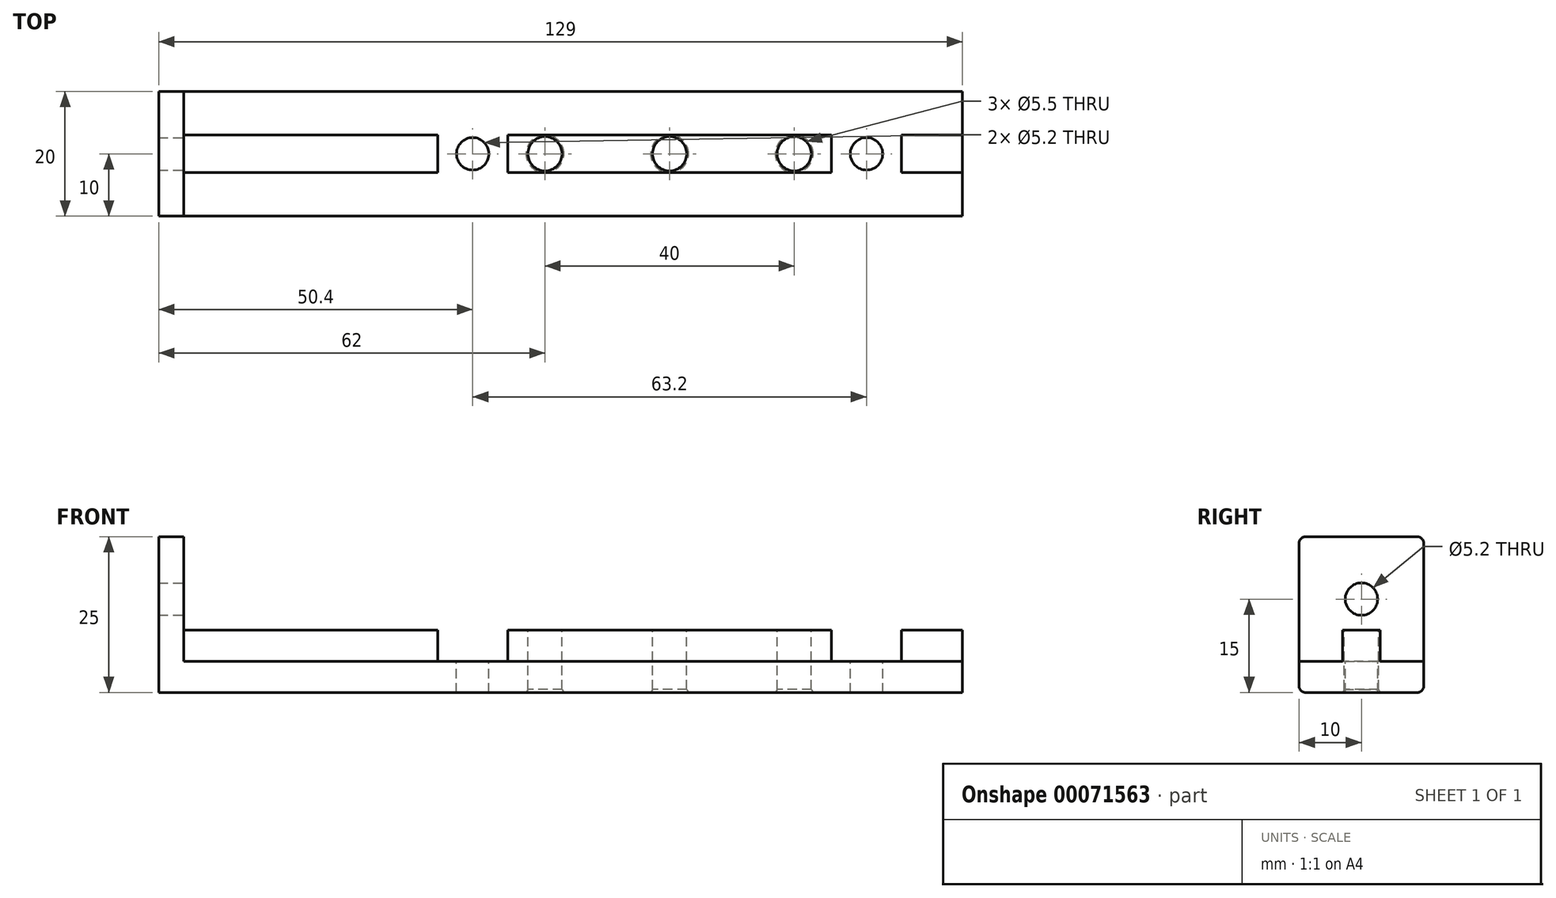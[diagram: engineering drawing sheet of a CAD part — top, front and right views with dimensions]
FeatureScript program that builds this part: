
annotation { "Feature Type Name" : "Feature", "Feature Type Description" : "" }
export const myFeature = defineFeature(function(context is Context, id is Id, definition is map)
    precondition{}
    {
        {
            var Q0;
            Q0=qCreatedBy(makeId("Top.planeOp"),FACE);
            var sketch = newSketch(context, id + "F0", { "sketchPlane" : qUnion([Q0])});
            skLineSegment(sketch, "E0.bottom", {"start": v(0, -10) * mm, "end": v(125, -10) * mm});
            skLineSegment(sketch, "E0.top", {"start": v(0, 10) * mm, "end": v(125, 10) * mm});
            skLineSegment(sketch, "E0.left", {"start": v(0, -10) * mm, "end": v(0, 10) * mm});
            skLineSegment(sketch, "E0.right", {"start": v(125, -10) * mm, "end": v(125, 10) * mm});
            skSolve(sketch);
        }
        {
            var Q0;
            Q0 = qSketchRegion(id + "F0", true);
            extrude(context, id + "F1", {"entities" : qUnion([Q0]), "depth" : 5 * mm});
        }
        {
            var Q0;
            Q0=makeQuery(id+"F1.opExtrude","CAP_FACE",FACE,{"disambiguationData":[OSD([sQuery(id+"F0.wireOp",EDGE,"E0.bottom"),sQuery(id+"F0.wireOp",EDGE,"E0.top"),sQuery(id+"F0.wireOp",EDGE,"E0.left"),sQuery(id+"F0.wireOp",EDGE,"E0.right")])],"isStart":false});
            var sketch = newSketch(context, id + "F2", { "sketchPlane" : qUnion([Q0])});
            skLineSegment(sketch, "E1.bottom", {"start": v(0, 3) * mm, "end": v(125, 3) * mm});
            skLineSegment(sketch, "E1.top", {"start": v(0, -3) * mm, "end": v(125, -3) * mm});
            skLineSegment(sketch, "E1.left", {"start": v(0, 3) * mm, "end": v(0, -3) * mm});
            skLineSegment(sketch, "E1.right", {"start": v(125, 3) * mm, "end": v(125, -3) * mm});
            skSolve(sketch);
        }
        {
            var Q0;
            Q0 = qSketchRegion(id + "F2", true);
            extrude(context, id + "F3", {"entities" : qUnion([Q0]), "operationType" : NewBodyOperationType.ADD, "depth" : 5 * mm});
        }
        {
            var Q0;
            Q0=makeQuery(id+"F3.opExtrude","CAP_FACE",FACE,{"disambiguationData":[OSD([sQuery(id+"F2.wireOp",EDGE,"E1.bottom"),sQuery(id+"F2.wireOp",EDGE,"E1.top"),sQuery(id+"F2.wireOp",EDGE,"E1.left"),sQuery(id+"F2.wireOp",EDGE,"E1.right")])],"isStart":false});
            var sketch = newSketch(context, id + "F4", { "sketchPlane" : qUnion([Q0])});
            skLineSegment(sketch, "E2", {"start": v(0, 0) * mm, "end": v(58, 0) * mm, "construction": true});
            skLineSegment(sketch, "E3", {"start": v(58, 0) * mm, "end": v(78, 0) * mm, "construction": true});
            skLineSegment(sketch, "E4", {"start": v(78, 0) * mm, "end": v(98, 0) * mm, "construction": true});
            skCircle(sketch, "E5", {"center": v(98, 0) * mm, "radius": 2.75 * mm});
            skCircle(sketch, "E6", {"center": v(78, 0) * mm, "radius": 2.75 * mm});
            skCircle(sketch, "E7", {"center": v(58, 0) * mm, "radius": 2.75 * mm});
            skSolve(sketch);
        }
        {
            var Q0;
            Q0 = qSketchRegion(id + "F4", true);
            extrude(context, id + "F5", {"entities" : qUnion([Q0]), "operationType" : NewBodyOperationType.REMOVE, "oppositeDirection" : true, "depth" : 25 * mm});
        }
        {
            var Q0;
            Q0=makeQuery(id+"F3.opExtrude","CAP_FACE",FACE,{"disambiguationData":[OSD([sQuery(id+"F2.wireOp",EDGE,"E1.bottom"),sQuery(id+"F2.wireOp",EDGE,"E1.top"),sQuery(id+"F2.wireOp",EDGE,"E1.left"),sQuery(id+"F2.wireOp",EDGE,"E1.right")])],"isStart":false});
            var sketch = newSketch(context, id + "F6", { "sketchPlane" : qUnion([Q0])});
            skLineSegment(sketch, "E8.bottom", {"start": v(104, 3) * mm, "end": v(115.2, 3) * mm});
            skLineSegment(sketch, "E8.top", {"start": v(104, -3) * mm, "end": v(115.2, -3) * mm});
            skLineSegment(sketch, "E8.left", {"start": v(104, 3) * mm, "end": v(104, -3) * mm});
            skLineSegment(sketch, "E8.right", {"start": v(115.2, 3) * mm, "end": v(115.2, -3) * mm});
            skLineSegment(sketch, "E9.bottom", {"start": v(40.8, 3) * mm, "end": v(52, 3) * mm});
            skLineSegment(sketch, "E9.top", {"start": v(40.8, -3) * mm, "end": v(52, -3) * mm});
            skLineSegment(sketch, "E9.left", {"start": v(40.8, 3) * mm, "end": v(40.8, -3) * mm});
            skLineSegment(sketch, "E9.right", {"start": v(52, 3) * mm, "end": v(52, -3) * mm});
            skLineSegment(sketch, "E10", {"start": v(58, 0) * mm, "end": v(52, 0) * mm, "construction": true});
            skLineSegment(sketch, "E11", {"start": v(98, 0) * mm, "end": v(104, 0) * mm, "construction": true});
            skSolve(sketch);
        }
        {
            var Q0;
            Q0 = qSketchRegion(id + "F6", true);
            var Q1;
            {var subQ0=sQuery(id+"F0.wireOp",EDGE,"E0.right");var subQ1=sQuery(id+"F0.wireOp",EDGE,"E0.left");var subQ2=sQuery(id+"F0.wireOp",EDGE,"E0.top");Q1=makeQuery(id+"F3.boolean.opBoolean","SPLIT",FACE,{"disambiguationData":[TD([makeQuery(id+"F1.opExtrude","SWEPT_FACE",FACE,{"disambiguationData":[OSD([subQ2])]})])],"derivedFrom":makeQuery(id+"F1.opExtrude","CAP_FACE",FACE,{"disambiguationData":[OSD([sQuery(id+"F0.wireOp",EDGE,"E0.bottom"),subQ2,subQ1,subQ0])],"isStart":false})});}
            extrude(context, id + "F7", {"entities" : qUnion([Q0]), "operationType" : NewBodyOperationType.REMOVE, "endBound" : BoundingType.UP_TO_SURFACE, "oppositeDirection" : true, "endBoundEntityFace" : qUnion([Q1]), "depth" : 25 * mm});
        }
        {
            var Q0;
            {var subQ0=sQuery(id+"F0.wireOp",EDGE,"E0.right");var subQ3=sQuery(id+"F0.wireOp",EDGE,"E0.left");var subQ5=sQuery(id+"F0.wireOp",EDGE,"E0.top");var subQ7=sQuery(id+"F0.wireOp",EDGE,"E0.bottom");var subQ8=makeQuery(id+"F1.opExtrude","CAP_FACE",FACE,{"disambiguationData":[OSD([subQ7,subQ5,subQ3,subQ0])],"isStart":false});Q0=makeQuery(id+"F7.boolean.opBoolean","MERGE",FACE,{"derivedFrom":[makeQuery(id+"F3.boolean.opBoolean","SPLIT",FACE,{"disambiguationData":[TD([makeQuery(id+"F1.opExtrude","SWEPT_FACE",FACE,{"disambiguationData":[OSD([subQ7])]})])],"derivedFrom":subQ8}),makeQuery(id+"F3.boolean.opBoolean","SPLIT",FACE,{"disambiguationData":[TD([makeQuery(id+"F1.opExtrude","SWEPT_FACE",FACE,{"disambiguationData":[OSD([subQ5])]})])],"derivedFrom":subQ8})],"fromTools":[makeQuery(id+"F7.opExtrude","CAP_FACE",FACE,{"disambiguationData":[OSD([sQuery(id+"F6.wireOp",EDGE,"E8.bottom"),sQuery(id+"F6.wireOp",EDGE,"E8.top"),sQuery(id+"F6.wireOp",EDGE,"E8.left"),sQuery(id+"F6.wireOp",EDGE,"E8.right")])],"isStart":false}),makeQuery(id+"F7.opExtrude","CAP_FACE",FACE,{"disambiguationData":[OSD([sQuery(id+"F6.wireOp",EDGE,"E9.bottom"),sQuery(id+"F6.wireOp",EDGE,"E9.top"),sQuery(id+"F6.wireOp",EDGE,"E9.left"),sQuery(id+"F6.wireOp",EDGE,"E9.right")])],"isStart":false})]});}
            var sketch = newSketch(context, id + "F8", { "sketchPlane" : qUnion([Q0])});
            skLineSegment(sketch, "E12", {"start": v(52, 0) * mm, "end": v(40.8, 0) * mm, "construction": true});
            skLineSegment(sketch, "E13", {"start": v(104, 0) * mm, "end": v(115.2, 0) * mm, "construction": true});
            skCircle(sketch, "E14", {"center": v(46.4, 0) * mm, "radius": 2.6 * mm});
            skCircle(sketch, "E15", {"center": v(109.6, 0) * mm, "radius": 2.6 * mm});
            skSolve(sketch);
        }
        {
            var Q0;
            Q0 = qSketchRegion(id + "F8", true);
            extrude(context, id + "F9", {"entities" : qUnion([Q0]), "operationType" : NewBodyOperationType.REMOVE, "endBound" : BoundingType.UP_TO_NEXT, "oppositeDirection" : true, "depth" : 25 * mm});
        }
        {
            var Q0;
            Q0=makeQuery(id+"F3.boolean.opBoolean","MERGE",FACE,{"derivedFrom":[makeQuery(id+"F1.opExtrude","SWEPT_FACE",FACE,{"disambiguationData":[OSD([sQuery(id+"F0.wireOp",EDGE,"E0.left")])]}),makeQuery(id+"F3.opExtrude","SWEPT_FACE",FACE,{"disambiguationData":[OSD([sQuery(id+"F2.wireOp",EDGE,"E1.left")])]})]});
            var sketch = newSketch(context, id + "F10", { "sketchPlane" : qUnion([Q0])});
            skLineSegment(sketch, "E16.bottom", {"start": v(-10, 0) * mm, "end": v(10, 0) * mm});
            skLineSegment(sketch, "E16.top", {"start": v(-10, 25) * mm, "end": v(10, 25) * mm});
            skLineSegment(sketch, "E16.left", {"start": v(-10, 0) * mm, "end": v(-10, 25) * mm});
            skLineSegment(sketch, "E16.right", {"start": v(10, 0) * mm, "end": v(10, 25) * mm});
            skCircle(sketch, "E17", {"center": v(0, 15) * mm, "radius": 2.6 * mm});
            skLineSegment(sketch, "E18", {"start": v(0, 15) * mm, "end": v(0, 25) * mm, "construction": true});
            skSolve(sketch);
        }
        {
            var Q0;
            {var subQ11=sQuery(id+"F10.wireOp",EDGE,"E16.top");Q0=makeQuery(id+"F10.imprint","IMPRINT",FACE,{"disambiguationData":[TD([[makeQuery(id+"F10.imprint","IMPRINT",EDGE,{"derivedFrom":subQ11}),-1.0]])]});}
            var Q1;
            {var subQ4=sQuery(id+"F10.wireOp",EDGE,"E16.bottom");Q1=makeQuery(id+"F10.imprint","IMPRINT",FACE,{"disambiguationData":[TD([[makeQuery(id+"F10.imprint","IMPRINT",EDGE,{"derivedFrom":subQ4}),-1.0]])]});}
            extrude(context, id + "F11", {"entities" : qUnion([Q0, Q1]), "operationType" : NewBodyOperationType.ADD, "depth" : 4 * mm});
        }
        {
            var Q0;
            Q0=makeQuery(id+"F11.opExtrude","SWEPT_EDGE",EDGE,{"disambiguationData":[OSD([sQuery(id+"F10.wireOp",EDGE,"E16.top"),sQuery(id+"F10.wireOp",EDGE,"E16.right")])]});
            var Q1;
            Q1=makeQuery(id+"F11.opExtrude","SWEPT_EDGE",EDGE,{"disambiguationData":[OSD([sQuery(id+"F10.wireOp",EDGE,"E16.top"),sQuery(id+"F10.wireOp",EDGE,"E16.left")])]});
            var Q2;
            Q2=makeQuery(id+"F11.boolean.opBoolean","MERGE",EDGE,{"derivedFrom":[makeQuery(id+"F1.opExtrude","CAP_EDGE",EDGE,{"disambiguationData":[OSD([sQuery(id+"F0.wireOp",EDGE,"E0.bottom")])],"isStart":true}),makeQuery(id+"F11.opExtrude","SWEPT_EDGE",EDGE,{"disambiguationData":[OSD([sQuery(id+"F10.wireOp",EDGE,"E16.bottom"),sQuery(id+"F10.wireOp",EDGE,"E16.right")])]})]});
            var Q3;
            Q3=makeQuery(id+"F11.boolean.opBoolean","MERGE",EDGE,{"derivedFrom":[makeQuery(id+"F1.opExtrude","CAP_EDGE",EDGE,{"disambiguationData":[OSD([sQuery(id+"F0.wireOp",EDGE,"E0.top")])],"isStart":true}),makeQuery(id+"F11.opExtrude","SWEPT_EDGE",EDGE,{"disambiguationData":[OSD([sQuery(id+"F10.wireOp",EDGE,"E16.bottom"),sQuery(id+"F10.wireOp",EDGE,"E16.left")])]})]});
            fillet(context, id + "F12", {"entities" : qUnion([Q0, Q1, Q2, Q3]), "radius" : 1 * mm, "tangentPropagation" : true, "allowEdgeOverflow" : false});
        }
        {
            var Q0;
            Q0=makeQuery(id+"F5.boolean.opBoolean","INTERSECT",EDGE,{"derivedFrom":[makeQuery(id+"F1.opExtrude","CAP_FACE",FACE,{"disambiguationData":[OSD([sQuery(id+"F0.wireOp",EDGE,"E0.bottom"),sQuery(id+"F0.wireOp",EDGE,"E0.top"),sQuery(id+"F0.wireOp",EDGE,"E0.left"),sQuery(id+"F0.wireOp",EDGE,"E0.right")])],"isStart":true}),makeQuery(id+"F5.opExtrude","SWEPT_FACE",FACE,{"disambiguationData":[OSD([sQuery(id+"F4.wireOp",EDGE,"E7")])]})]});
            var Q1;
            Q1=makeQuery(id+"F5.boolean.opBoolean","INTERSECT",EDGE,{"derivedFrom":[makeQuery(id+"F1.opExtrude","CAP_FACE",FACE,{"disambiguationData":[OSD([sQuery(id+"F0.wireOp",EDGE,"E0.bottom"),sQuery(id+"F0.wireOp",EDGE,"E0.top"),sQuery(id+"F0.wireOp",EDGE,"E0.left"),sQuery(id+"F0.wireOp",EDGE,"E0.right")])],"isStart":true}),makeQuery(id+"F5.opExtrude","SWEPT_FACE",FACE,{"disambiguationData":[OSD([sQuery(id+"F4.wireOp",EDGE,"E6")])]})]});
            var Q2;
            Q2=makeQuery(id+"F5.boolean.opBoolean","INTERSECT",EDGE,{"derivedFrom":[makeQuery(id+"F1.opExtrude","CAP_FACE",FACE,{"disambiguationData":[OSD([sQuery(id+"F0.wireOp",EDGE,"E0.bottom"),sQuery(id+"F0.wireOp",EDGE,"E0.top"),sQuery(id+"F0.wireOp",EDGE,"E0.left"),sQuery(id+"F0.wireOp",EDGE,"E0.right")])],"isStart":true}),makeQuery(id+"F5.opExtrude","SWEPT_FACE",FACE,{"disambiguationData":[OSD([sQuery(id+"F4.wireOp",EDGE,"E5")])]})]});
            chamfer(context, id + "F13", {"entities" : qUnion([Q0, Q1, Q2]), "chamferType" : ChamferType.OFFSET_ANGLE, "width" : .5 * mm, "oppositeDirection" : true, "angle" : 30 * degree, "tangentPropagation" : true});
        }
    });
